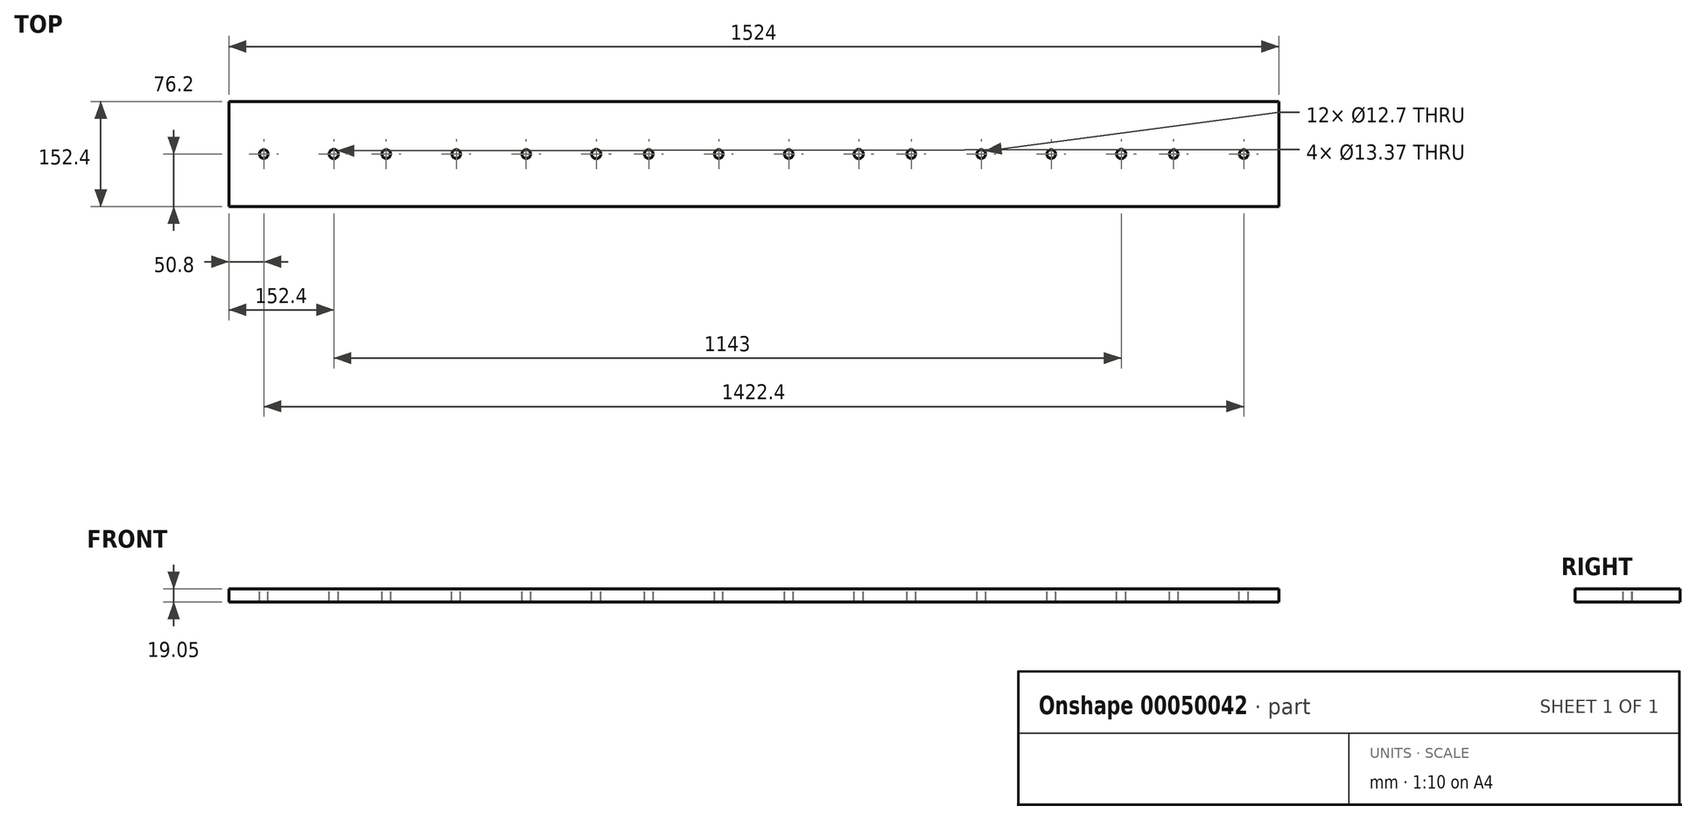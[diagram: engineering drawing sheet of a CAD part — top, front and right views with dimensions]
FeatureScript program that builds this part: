
annotation { "Feature Type Name" : "Feature", "Feature Type Description" : "" }
export const myFeature = defineFeature(function(context is Context, id is Id, definition is map)
    precondition{}
    {
        {
            var Q0;
            Q0=qCreatedBy(makeId("Top.planeOp"),FACE);
            var sketch = newSketch(context, id + "F0", { "sketchPlane" : qUnion([Q0])});
            skLineSegment(sketch, "E0.bottom", {"start": v(0, 0) * mm, "end": v(1524, 0) * mm});
            skLineSegment(sketch, "E0.top", {"start": v(0, 152.4) * mm, "end": v(1524, 152.4) * mm});
            skLineSegment(sketch, "E0.left", {"start": v(0, 0) * mm, "end": v(0, 152.4) * mm});
            skLineSegment(sketch, "E0.right", {"start": v(1524, 0) * mm, "end": v(1524, 152.4) * mm});
            skSolve(sketch);
        }
        {
            var Q0;
            Q0=makeQuery(id+"F0.imprint","IMPRINT",FACE,{"disambiguationData":[TD([[makeQuery(id+"F0.imprint","IMPRINT",EDGE,{"derivedFrom":sQuery(id+"F0.wireOp",EDGE,"E0.bottom")}),1.0]])]});
            extrude(context, id + "F1", {"entities" : qUnion([Q0]), "depth" : 19.05 * mm});
        }
        {
            var Q0;
            Q0=makeQuery(id+"F1.opExtrude","CAP_FACE",FACE,{"disambiguationData":[OSD([sQuery(id+"F0.wireOp",EDGE,"E0.bottom"),sQuery(id+"F0.wireOp",EDGE,"E0.top"),sQuery(id+"F0.wireOp",EDGE,"E0.left"),sQuery(id+"F0.wireOp",EDGE,"E0.right")])],"isStart":false});
            var sketch = newSketch(context, id + "F2", { "sketchPlane" : qUnion([Q0])});
            skCircle(sketch, "E1", {"center": v(50.8, 76.2) * mm, "radius": 6.35 * mm});
            skCircle(sketch, "E2", {"center": v(152.4, 76.2) * mm, "radius": 6.68 * mm});
            skCircle(sketch, "E3", {"center": v(228.6, 76.2) * mm, "radius": 6.35 * mm});
            skCircle(sketch, "E4", {"center": v(330.2, 76.2) * mm, "radius": 6.35 * mm});
            skCircle(sketch, "E5.1.0.0", {"center": v(533.4, 76.2) * mm, "radius": 6.68 * mm});
            skCircle(sketch, "E5.1.0.1", {"center": v(431.8, 76.2) * mm, "radius": 6.35 * mm});
            skCircle(sketch, "E5.1.0.2", {"center": v(609.6, 76.2) * mm, "radius": 6.35 * mm});
            skCircle(sketch, "E5.1.0.3", {"center": v(711.2, 76.2) * mm, "radius": 6.35 * mm});
            skCircle(sketch, "E5.2.0.0", {"center": v(914.4, 76.2) * mm, "radius": 6.68 * mm});
            skCircle(sketch, "E5.2.0.1", {"center": v(812.8, 76.2) * mm, "radius": 6.35 * mm});
            skCircle(sketch, "E5.2.0.2", {"center": v(990.6, 76.2) * mm, "radius": 6.35 * mm});
            skCircle(sketch, "E5.2.0.3", {"center": v(1092.2, 76.2) * mm, "radius": 6.35 * mm});
            skLineSegment(sketch, "E5.direction1", {"start": v(152.4, 76.2) * mm, "end": v(533.4, 76.2) * mm, "construction": true});
            skCircle(sketch, "E6.1.0.0", {"center": v(1295.4, 76.2) * mm, "radius": 6.68 * mm});
            skCircle(sketch, "E6.1.0.1", {"center": v(1193.8, 76.2) * mm, "radius": 6.35 * mm});
            skCircle(sketch, "E6.1.0.2", {"center": v(1371.6, 76.2) * mm, "radius": 6.35 * mm});
            skCircle(sketch, "E6.1.0.3", {"center": v(1473.2, 76.2) * mm, "radius": 6.35 * mm});
            skLineSegment(sketch, "E6.direction1", {"start": v(914.4, 76.2) * mm, "end": v(1295.4, 76.2) * mm, "construction": true});
            skSolve(sketch);
        }
        {
            var Q0;
            Q0=makeQuery(id+"F2.imprint","IMPRINT",FACE,{"disambiguationData":[TD([[makeQuery(id+"F2.imprint","IMPRINT",EDGE,{"derivedFrom":sQuery(id+"F2.wireOp",EDGE,"E1")}),1.0]])]});
            var Q1;
            Q1=makeQuery(id+"F2.imprint","IMPRINT",FACE,{"disambiguationData":[TD([[makeQuery(id+"F2.imprint","IMPRINT",EDGE,{"derivedFrom":sQuery(id+"F2.wireOp",EDGE,"E2")}),1.0]])]});
            var Q2;
            Q2=makeQuery(id+"F2.imprint","IMPRINT",FACE,{"disambiguationData":[TD([[makeQuery(id+"F2.imprint","IMPRINT",EDGE,{"derivedFrom":sQuery(id+"F2.wireOp",EDGE,"E3")}),1.0]])]});
            var Q3;
            Q3=makeQuery(id+"F2.imprint","IMPRINT",FACE,{"disambiguationData":[TD([[makeQuery(id+"F2.imprint","IMPRINT",EDGE,{"derivedFrom":sQuery(id+"F2.wireOp",EDGE,"E4")}),1.0]])]});
            var Q4;
            Q4=makeQuery(id+"F2.imprint","IMPRINT",FACE,{"disambiguationData":[TD([[makeQuery(id+"F2.imprint","IMPRINT",EDGE,{"derivedFrom":sQuery(id+"F2.wireOp",EDGE,"E5.1.0.1")}),1.0]])]});
            var Q5;
            Q5=makeQuery(id+"F2.imprint","IMPRINT",FACE,{"disambiguationData":[TD([[makeQuery(id+"F2.imprint","IMPRINT",EDGE,{"derivedFrom":sQuery(id+"F2.wireOp",EDGE,"E5.1.0.0")}),1.0]])]});
            var Q6;
            Q6=makeQuery(id+"F2.imprint","IMPRINT",FACE,{"disambiguationData":[TD([[makeQuery(id+"F2.imprint","IMPRINT",EDGE,{"derivedFrom":sQuery(id+"F2.wireOp",EDGE,"E5.1.0.2")}),1.0]])]});
            var Q7;
            Q7=makeQuery(id+"F2.imprint","IMPRINT",FACE,{"disambiguationData":[TD([[makeQuery(id+"F2.imprint","IMPRINT",EDGE,{"derivedFrom":sQuery(id+"F2.wireOp",EDGE,"E5.1.0.3")}),1.0]])]});
            var Q8;
            Q8=makeQuery(id+"F2.imprint","IMPRINT",FACE,{"disambiguationData":[TD([[makeQuery(id+"F2.imprint","IMPRINT",EDGE,{"derivedFrom":sQuery(id+"F2.wireOp",EDGE,"E5.2.0.1")}),1.0]])]});
            var Q9;
            Q9=makeQuery(id+"F2.imprint","IMPRINT",FACE,{"disambiguationData":[TD([[makeQuery(id+"F2.imprint","IMPRINT",EDGE,{"derivedFrom":sQuery(id+"F2.wireOp",EDGE,"E5.2.0.0")}),1.0]])]});
            var Q10;
            Q10=makeQuery(id+"F2.imprint","IMPRINT",FACE,{"disambiguationData":[TD([[makeQuery(id+"F2.imprint","IMPRINT",EDGE,{"derivedFrom":sQuery(id+"F2.wireOp",EDGE,"E5.2.0.2")}),1.0]])]});
            var Q11;
            Q11=makeQuery(id+"F2.imprint","IMPRINT",FACE,{"disambiguationData":[TD([[makeQuery(id+"F2.imprint","IMPRINT",EDGE,{"derivedFrom":sQuery(id+"F2.wireOp",EDGE,"E5.2.0.3")}),1.0]])]});
            var Q12;
            Q12=makeQuery(id+"F2.imprint","IMPRINT",FACE,{"disambiguationData":[TD([[makeQuery(id+"F2.imprint","IMPRINT",EDGE,{"derivedFrom":sQuery(id+"F2.wireOp",EDGE,"E6.1.0.1")}),1.0]])]});
            var Q13;
            Q13=makeQuery(id+"F2.imprint","IMPRINT",FACE,{"disambiguationData":[TD([[makeQuery(id+"F2.imprint","IMPRINT",EDGE,{"derivedFrom":sQuery(id+"F2.wireOp",EDGE,"E6.1.0.0")}),1.0]])]});
            var Q14;
            Q14=makeQuery(id+"F2.imprint","IMPRINT",FACE,{"disambiguationData":[TD([[makeQuery(id+"F2.imprint","IMPRINT",EDGE,{"derivedFrom":sQuery(id+"F2.wireOp",EDGE,"E6.1.0.2")}),1.0]])]});
            var Q15;
            Q15=makeQuery(id+"F2.imprint","IMPRINT",FACE,{"disambiguationData":[TD([[makeQuery(id+"F2.imprint","IMPRINT",EDGE,{"derivedFrom":sQuery(id+"F2.wireOp",EDGE,"E6.1.0.3")}),1.0]])]});
            extrude(context, id + "F3", {"entities" : qUnion([Q0, Q1, Q2, Q3, Q4, Q5, Q6, Q7, Q8, Q9, Q10, Q11, Q12, Q13, Q14, Q15]), "operationType" : NewBodyOperationType.REMOVE, "endBound" : BoundingType.THROUGH_ALL, "oppositeDirection" : true, "depth" : 25.4 * mm});
        }
    });
